FCSTD DOCUMENT  (FreeCAD 2023.131R26244 +5365 (Git))
Label: Parameters
License: All rights reserved
LicenseURL: http://en.wikipedia.org/wiki/All_rights_reserved
objects: Spreadsheet::Sheet×1

FEATURE [Spreadsheet::Sheet] Spreadsheet  label="Parameters"
  PythonMode = false
  ShowCells = 0
  TreeRank = 1
  cells = A1=Overall Diameter; B1(Outer_Diameter)=75; C1=The outer diameter of the handles of the grinder. The base of the stand will be wider.; A2=Overlap Spacing; B2(Overlap_Spacing)=0.5; C2=The distance between the inner ring of the top and outer ring of the bottom of the grinder.; A3=Grinder Diameter; B3(Grinder_Diameter)=65; C3=The internal diameter of the grinder area.; A4=Wall Thickness; B4(Wall_Thickness)=2; C4=How thick walls are in general. Used throughout.; A5=Tooth Height; B5(Tooth_Height)=10; C5=The height of the teeth in the grinder.; A6=Tooth Spacing; B6(Tooth_Spacing)=0.35; C6=The distance between the rings in the grinder.; A7=Spice Hole Diameter; B7(Spice_Hole_Diameter)=4; C7=The diameter of the holes in the bottom half of the grinder that let the ground spice fall into the cone.; A8=Spice Cone Length; B8(Spice_Cone_Height)=110; C8=The overall length of the cone that will be filled with spice. This includes the filter.; A9=Spice Cone Smallest Diameter; B9(Spice_Cone_Min)=6; C9=The diameter of the cone at its narrowest part.; A10=Spice Cone Largest Diameter; B10(Spice_Cone_Max)=12.5; C10=The diameter of the cone at its widest part.; A12=Top Handle Height; B12(Top_Handle_Height)=15; C12=How thick the top of the grinder is. This is the part that fits in the hand.; A14=Middle Outer Diameter; B14(Middle_Outer_Diameter)==Grinder_Diameter + 2 * Wall_Thickness; A15=Middle Height; B15(Middle_Height)==Tooth_Height + Wall_Thickness * 2; A16=Middle Side Post Diameter; B16(Middle_Side_Post_Diameter)=10; C16=The diameter of the posts on the side of the middle part that align the funnel.; A17=Middle Side Post Height; B17(Middle_Side_Post_Height)==Middle_Height; C17=The height of the posts on the side of the middle part that align the funnel.; A18=Center Post Diameter; B18(Center_Post_Diameter)=10; A20=Cone Inner Diameter; B20(Cone_Inner_Diameter)==Middle_Outer_Diameter + 2 * Overlap_Spacing; A21=Cone Outer Diamter; B21(Cone_Outer_Diameter)==Cone_Inner_Diameter + Cone_Side_Post_Diameter + 4 * Wall_Thickness; A22=Code Side Post Diameter; B22(Cone_Side_Post_Diameter)==Middle_Side_Post_Diameter * Cone_Inner_Diameter / Middle_Outer_Diameter; A23=Cone Side Angle; B23(Cone_Angle)=8.5; A24=Cone Collection Height; B24(Cone_Collection_Height)=30; A25=Cone Insert Length; B25(Cone_Insert_Height)=15; A26=Cone Insert Max Width; B26(Cone_Insert_Width)==Spice_Cone_Max; A27=Cone Collection Diameter; B27(Cone_Collection_Diameter)==sqrt(pow(Cone_Outer_Diameter / 2, 2) - pow(Cone_Outer_Diameter * sin(22.3) / 2, 2)) * 2; A29=Tooth Ring Count; B29(Tooth_Rings)=5; C29=Should be an odd number. The bottom will have ceil( n / 2 ) rings and the top with have floor( n / 2 ) rings.; A30=Top Tooth Ring Count; B30(Top_Tooth_Rings)==floor(Tooth_Rings / 2); C30=The number of tooth rings on the top of the grinder. This should be the same as the number of rings in the bottom.; A31=Bottom Tooth Ring Count; B31(Bottom_Tooth_Rings)==ceil(Tooth_Rings / 2); C31=The number of tooth rings on the bottom of the grinder. This should be the same as the number of rings in the top.; A32=Tooth Ring Diameter; B32(Tooth_Ring_Diameter)==(Grinder_Diameter - Center_Post_Diameter) / Tooth_Rings; C32=The difference in diameter between neighboring tooth rings.; B34=Inner; C34=Center; D34=Outer; E34=Teeth; A35=Top Tooth Ring #1; B35(Top_Ring1_Inner)==Top_Ring1_Center - Tooth_Ring_Diameter / 2; C35(Top_Ring1_Center)==Middle_Ring1_Center + Tooth_Ring_Diameter; D35(Top_Ring1_Outer)==Top_Ring1_Center + Tooth_Ring_Diameter / 2; E35(Top_Ring1_Teeth)=10; A36=Top Tooth Ring #2; B36(Top_Ring2_Inner)==Top_Ring2_Center - Tooth_Ring_Diameter / 2; C36(Top_Ring2_Center)==Top_Tooth_Rings >= 2 ? Middle_Ring2_Center + Tooth_Ring_Diameter : 0; D36(Top_Ring2_Outer)==Top_Ring2_Center + Tooth_Ring_Diameter / 2; E36(Top_Ring2_Teeth)=16; A37=Top Tooth Ring #3; B37(Top_Ring3_Inner)==Top_Ring3_Center - Tooth_Ring_Diameter / 2; C37(Top_Ring3_Center)==Top_Tooth_Rings >= 3 ? Middle_Ring3_Center + Tooth_Ring_Diameter : 0; D37(Top_Ring3_Outer)==Top_Ring3_Center + Tooth_Ring_Diameter / 2; E37(Top_Ring3_Teeth)=22; A38=Top Tooth Ring #4; B38(Top_Ring4_Inner)==Top_Ring4_Center - Tooth_Ring_Diameter / 2; C38(Top_Ring4_Center)==Top_Tooth_Rings >= 4 ? Middle_Ring4_Center + Tooth_Ring_Diameter : 0; D38(Top_Ring4_Outer)==Top_Ring4_Center + Tooth_Ring_Diameter / 2; E38(Top_Ring4_Teeth)=30; A39=Top Tooth Ring #5; B39(Top_Ring5_Inner)==Top_Ring5_Center - Tooth_Ring_Diameter / 2; C39(Top_Ring5_Center)==Top_Tooth_Rings >= 5 ? Middle_Ring5_Center + Tooth_Ring_Diameter : 0; D39(Top_Ring5_Outer)==Top_Ring5_Center + Tooth_Ring_Diameter / 2; E39(Top_Ring5_Teeth)=40; B41=Inner; C41=Center; D41=Outer; E41=13; F41=Tooth Y-Angle; G41=Hole Y-Angle; H41=Tooth Width; I41=Side Angle; A42=Middle Tooth Ring #1; B42(Middle_Ring1_Inner)==Middle_Ring1_Center - Tooth_Ring_Diameter / 2 + Tooth_Spacing; C42(Middle_Ring1_Center)==Center_Post_Diameter; D42(Middle_Ring1_Outer)==Middle_Ring1_Center + Tooth_Ring_Diameter / 2 - Tooth_Spacing; E42(Middle_Ring1_Teeth)=5; F42(Middle_Ring1_Tooth_Angle)=15; G42(Middle_Ring1_Hole_Angle)==Middle_Ring1_Tooth_Angle + 180; H42(Middle_Ring1_Tooth_Width)==pi * Middle_Ring1_Center / Middle_Ring1_Teeth + 1; I42(Middle_Ring1_Side_Angle)=8; A43=Middle Tooth Ring #2; B43(Middle_Ring2_Inner)==Middle_Ring2_Center - Tooth_Ring_Diameter / 2 + Tooth_Spacing; C43(Middle_Ring2_Center)==Bottom_Tooth_Rings >= 2 ? Top_Ring1_Center + Tooth_Ring_Diameter : 0; D43(Middle_Ring2_Outer)==Middle_Ring2_Center + Tooth_Ring_Diameter / 2; E43(Middle_Ring2_Teeth)=13; F43(Middle_Ring2_Tooth_Angle)=23; G43(Middle_Ring2_Hole_Angle)==Middle_Ring2_Tooth_Angle + 180; H43(Middle_Ring2_Tooth_Width)==pi * Middle_Ring2_Center / Middle_Ring2_Teeth + 1; I43(Middle_Ring2_Side_Angle)=12.5; A44=Middle Tooth Ring #3; B44(Middle_Ring3_Inner)==Middle_Ring3_Center - Tooth_Ring_Diameter / 2 + Tooth_Spacing; C44(Middle_Ring3_Center)==Bottom_Tooth_Rings >= 3 ? Top_Ring2_Center + Tooth_Ring_Diameter : 0; D44(Middle_Ring3_Outer)==Middle_Ring3_Center + Tooth_Ring_Diameter / 2 - Tooth_Spacing; E44(Middle_Ring3_Teeth)=17; F44(Middle_Ring3_Tooth_Angle)=31; G44(Middle_Ring3_Hole_Angle)==Middle_Ring3_Tooth_Angle + 180; H44(Middle_Ring3_Tooth_Width)==pi * Middle_Ring3_Center / Middle_Ring3_Teeth + 1; I44(Middle_Ring3_Side_Angle)=13; A45=Middle Tooth Ring #4; B45(Middle_Ring4_Inner)==Middle_Ring4_Center - Tooth_Ring_Diameter / 2 + Tooth_Spacing; C45(Middle_Ring4_Center)==Bottom_Tooth_Rings >= 4 ? Top_Ring3_Center + Tooth_Ring_Diameter : 0; D45(Middle_Ring4_Outer)==Middle_Ring4_Center + Tooth_Ring_Diameter / 2 - Tooth_Spacing; E45(Middle_Ring4_Teeth)=11; F45(Middle_Ring4_Tooth_Angle)=45; G45(Middle_Ring4_Hole_Angle)==Middle_Ring4_Tooth_Angle + 180; H45(Middle_Ring4_Tooth_Width)==pi * Middle_Ring4_Center / Middle_Ring4_Teeth + 1; I45(Middle_Ring4_Side_Angle)=; A46=Middle Tooth Ring #5; B46(Middle_Ring5_Inner)==Middle_Ring5_Center - Tooth_Ring_Diameter / 2 + Tooth_Spacing; C46(Middle_Ring5_Center)==Bottom_Tooth_Rings >= 5 ? Top_Ring4_Center + Tooth_Ring_Diameter : 0; D46(Middle_Ring5_Outer)==Middle_Ring5_Center + Tooth_Ring_Diameter / 2 - Tooth_Spacing; E46(Middle_Ring5_Teeth)=13; F46(Middle_Ring5_Tooth_Angle)=51; G46(Middle_Ring5_Hole_Angle)==Middle_Ring5_Tooth_Angle + 180; H46(Middle_Ring5_Tooth_Width)==pi * Middle_Ring5_Center / Middle_Ring5_Teeth + 1; I46(Middle_Ring5_Side_Angle)=
